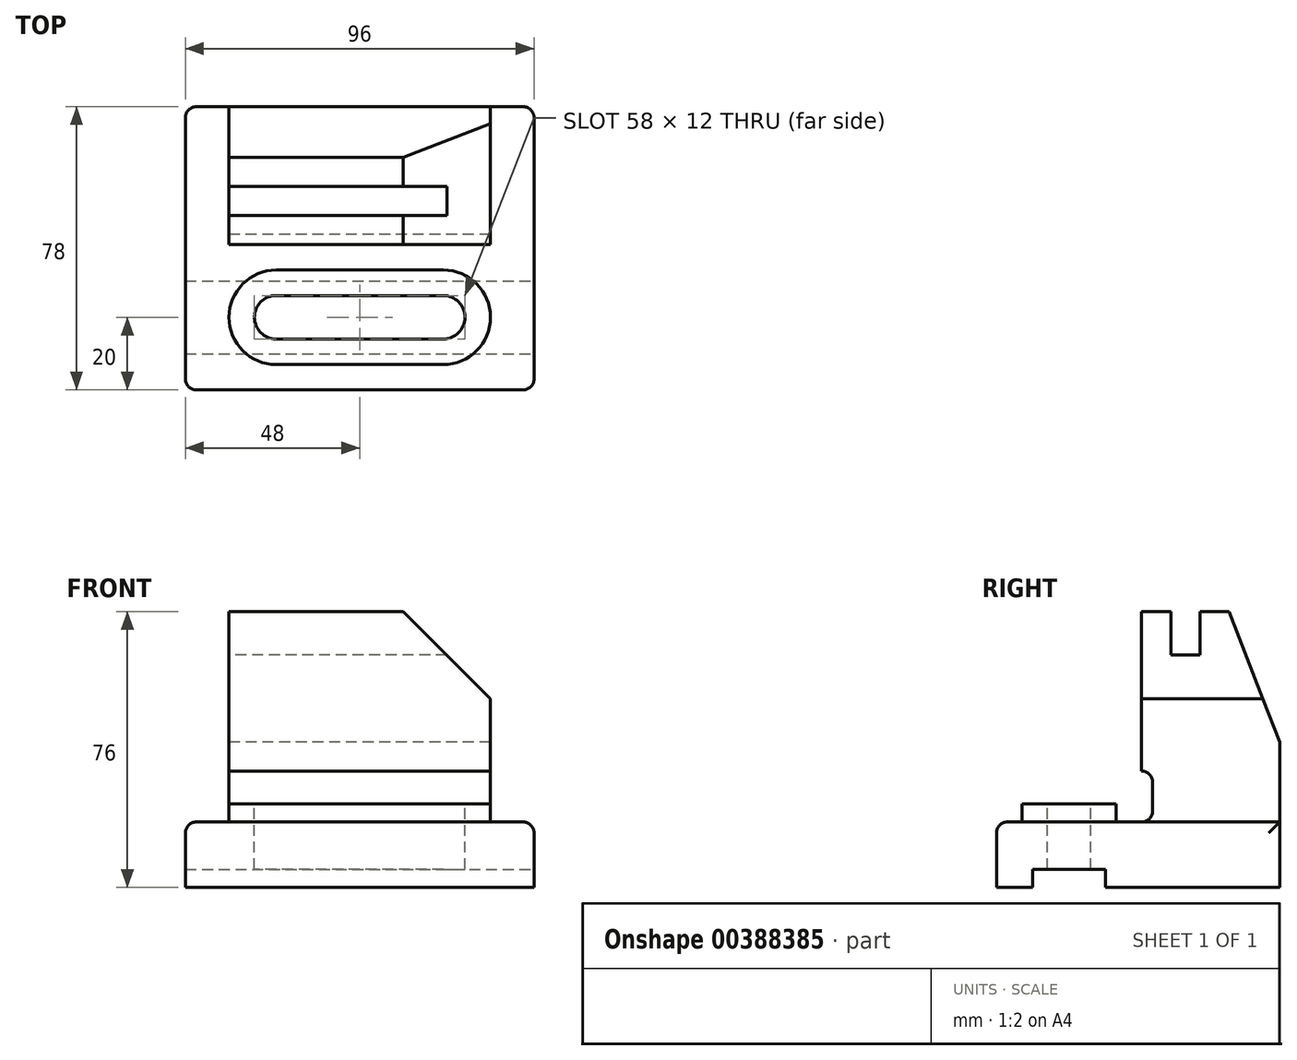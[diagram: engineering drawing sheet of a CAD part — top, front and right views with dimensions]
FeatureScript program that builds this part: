
annotation { "Feature Type Name" : "Feature", "Feature Type Description" : "" }
export const myFeature = defineFeature(function(context is Context, id is Id, definition is map)
    precondition{}
    {
        {
            var Q0;
            Q0=qCreatedBy(makeId("Top.planeOp"),FACE);
            var sketch = newSketch(context, id + "F0", { "sketchPlane" : qUnion([Q0])});
            skLineSegment(sketch, "E0.bottom", {"start": v(0, 0) * mm, "end": v(96, 0) * mm});
            skLineSegment(sketch, "E0.top", {"start": v(0, 78) * mm, "end": v(96, 78) * mm});
            skLineSegment(sketch, "E0.left", {"start": v(0, 0) * mm, "end": v(0, 78) * mm});
            skLineSegment(sketch, "E0.right", {"start": v(96, 0) * mm, "end": v(96, 78) * mm});
            skSolve(sketch);
        }
        {
            var Q0;
            Q0 = qSketchRegion(id + "F0", true);
            extrude(context, id + "F1", {"entities" : qUnion([Q0]), "depth" : 18 * mm});
        }
        {
            var Q0;
            Q0=makeQuery(id+"F1.opExtrude","CAP_FACE",FACE,{"disambiguationData":[OSD([sQuery(id+"F0.wireOp",EDGE,"E0.bottom"),sQuery(id+"F0.wireOp",EDGE,"E0.top"),sQuery(id+"F0.wireOp",EDGE,"E0.left"),sQuery(id+"F0.wireOp",EDGE,"E0.right")])],"isStart":false});
            var sketch = newSketch(context, id + "F2", { "sketchPlane" : qUnion([Q0])});
            skLineSegment(sketch, "E1.bottom", {"start": v(12, 78) * mm, "end": v(84, 78) * mm});
            skLineSegment(sketch, "E1.top", {"start": v(12, 40) * mm, "end": v(84, 40) * mm});
            skLineSegment(sketch, "E1.left", {"start": v(12, 78) * mm, "end": v(12, 40) * mm});
            skLineSegment(sketch, "E1.right", {"start": v(84, 78) * mm, "end": v(84, 40) * mm});
            skSolve(sketch);
        }
        {
            var Q0;
            Q0=makeQuery(id+"F1.opExtrude","CAP_FACE",FACE,{"disambiguationData":[OSD([sQuery(id+"F0.wireOp",EDGE,"E0.bottom"),sQuery(id+"F0.wireOp",EDGE,"E0.top"),sQuery(id+"F0.wireOp",EDGE,"E0.left"),sQuery(id+"F0.wireOp",EDGE,"E0.right")])],"isStart":true});
            cPlane(context, id + "F3", {"entities" : qUnion([Q0]), "cplaneType" : CPlaneType.OFFSET, "offset" : 76 * mm, "oppositeDirection" : true, "width" : 150 * mm, "height" : 150 * mm});
        }
        {
            var Q0;
            Q0=makeQuery(id+"F2.imprint","IMPRINT",FACE,{"disambiguationData":[TD([[makeQuery(id+"F2.imprint","IMPRINT",EDGE,{"derivedFrom":sQuery(id+"F2.wireOp",EDGE,"E1.bottom")}),-1.0]])]});
            var Q1;
            Q1=qCreatedBy(id+"F3.planeOp",FACE);
            extrude(context, id + "F4", {"entities" : qUnion([Q0]), "operationType" : NewBodyOperationType.ADD, "endBound" : BoundingType.UP_TO_SURFACE, "endBoundEntityFace" : qUnion([Q1]), "depth" : 9 * mm});
        }
        {
            var Q0;
            Q0=makeQuery(id+"F4.boolean.opBoolean","MERGE",FACE,{"derivedFrom":[makeQuery(id+"F1.opExtrude","SWEPT_FACE",FACE,{"disambiguationData":[OSD([sQuery(id+"F0.wireOp",EDGE,"E0.top")])]}),makeQuery(id+"F4.opExtrude","SWEPT_FACE",FACE,{"disambiguationData":[OSD([sQuery(id+"F2.wireOp",EDGE,"E1.bottom")])]})]});
            var sketch = newSketch(context, id + "F5", { "sketchPlane" : qUnion([Q0])});
            skLineSegment(sketch, "E2", {"start": v(-84, 76) * mm, "end": v(-60, 76) * mm});
            skLineSegment(sketch, "E3", {"start": v(-60, 76) * mm, "end": v(-84, 52) * mm});
            skLineSegment(sketch, "E4", {"start": v(-84, 52) * mm, "end": v(-84, 76) * mm});
            skSolve(sketch);
        }
        {
            var Q0;
            Q0 = qSketchRegion(id + "F5", true);
            var Q1;
            Q1=makeQuery(id+"F4.opExtrude","SWEPT_FACE",FACE,{"disambiguationData":[OSD([sQuery(id+"F2.wireOp",EDGE,"E1.top")])]});
            extrude(context, id + "F6", {"entities" : qUnion([Q0]), "operationType" : NewBodyOperationType.REMOVE, "endBound" : BoundingType.UP_TO_SURFACE, "oppositeDirection" : true, "endBoundEntityFace" : qUnion([Q1]), "depth" : 25 * mm});
        }
        {
            var Q0;
            Q0=makeQuery(id+"F4.opExtrude","SWEPT_FACE",FACE,{"disambiguationData":[OSD([sQuery(id+"F2.wireOp",EDGE,"E1.left")])]});
            var sketch = newSketch(context, id + "F7", { "sketchPlane" : qUnion([Q0])});
            skLineSegment(sketch, "E5.bottom", {"start": v(-48, 76) * mm, "end": v(-56, 76) * mm});
            skLineSegment(sketch, "E5.top", {"start": v(-48, 64) * mm, "end": v(-56, 64) * mm});
            skLineSegment(sketch, "E5.left", {"start": v(-48, 76) * mm, "end": v(-48, 64) * mm});
            skLineSegment(sketch, "E5.right", {"start": v(-56, 76) * mm, "end": v(-56, 64) * mm});
            skSolve(sketch);
        }
        {
            var Q0;
            Q0 = qSketchRegion(id + "F7", true);
            extrude(context, id + "F8", {"entities" : qUnion([Q0]), "operationType" : NewBodyOperationType.REMOVE, "endBound" : BoundingType.UP_TO_NEXT, "oppositeDirection" : true, "depth" : 25 * mm});
        }
        {
            var Q0;
            Q0=makeQuery(id+"F4.opExtrude","SWEPT_FACE",FACE,{"disambiguationData":[OSD([sQuery(id+"F2.wireOp",EDGE,"E1.left")])]});
            var sketch = newSketch(context, id + "F9", { "sketchPlane" : qUnion([Q0])});
            skLineSegment(sketch, "E6", {"start": v(-64, 76) * mm, "end": v(-78, 76) * mm});
            skLineSegment(sketch, "E7", {"start": v(-78, 76) * mm, "end": v(-78, 40) * mm});
            skLineSegment(sketch, "E8", {"start": v(-78, 40) * mm, "end": v(-64, 76) * mm});
            skSolve(sketch);
        }
        {
            var Q0;
            Q0 = qSketchRegion(id + "F9", true);
            extrude(context, id + "F10", {"entities" : qUnion([Q0]), "operationType" : NewBodyOperationType.REMOVE, "endBound" : BoundingType.UP_TO_NEXT, "oppositeDirection" : true, "depth" : 25 * mm});
        }
        {
            var Q0;
            Q0=makeQuery(id+"F1.opExtrude","SWEPT_FACE",FACE,{"disambiguationData":[OSD([sQuery(id+"F0.wireOp",EDGE,"E0.right")])]});
            var sketch = newSketch(context, id + "F11", { "sketchPlane" : qUnion([Q0])});
            skLineSegment(sketch, "E9.bottom", {"start": v(10, 0) * mm, "end": v(30, 0) * mm});
            skLineSegment(sketch, "E9.top", {"start": v(10, 5) * mm, "end": v(30, 5) * mm});
            skLineSegment(sketch, "E9.left", {"start": v(10, 0) * mm, "end": v(10, 5) * mm});
            skLineSegment(sketch, "E9.right", {"start": v(30, 0) * mm, "end": v(30, 5) * mm});
            skPoint(sketch, "E10", {"position": v(20, 5) * mm});
            skSolve(sketch);
        }
        {
            var Q0;
            Q0 = qSketchRegion(id + "F11", true);
            extrude(context, id + "F12", {"entities" : qUnion([Q0]), "operationType" : NewBodyOperationType.REMOVE, "endBound" : BoundingType.THROUGH_ALL, "oppositeDirection" : true, "depth" : 25 * mm});
        }
        {
            var Q0;
            Q0=makeQuery(id+"F1.opExtrude","CAP_FACE",FACE,{"disambiguationData":[OSD([sQuery(id+"F0.wireOp",EDGE,"E0.bottom"),sQuery(id+"F0.wireOp",EDGE,"E0.top"),sQuery(id+"F0.wireOp",EDGE,"E0.left"),sQuery(id+"F0.wireOp",EDGE,"E0.right")])],"isStart":false});
            var sketch = newSketch(context, id + "F13", { "sketchPlane" : qUnion([Q0])});
            skLineSegment(sketch, "E11.bottom", {"start": v(25, 33) * mm, "end": v(71, 33) * mm});
            skLineSegment(sketch, "E11.top", {"start": v(25, 7) * mm, "end": v(71, 7) * mm});
            skLineSegment(sketch, "E11.left", {"start": v(25, 33) * mm, "end": v(25, 7) * mm});
            skLineSegment(sketch, "E11.right", {"start": v(71, 33) * mm, "end": v(71, 7) * mm});
            skLineSegment(sketch, "E12", {"start": v(25, 20) * mm, "end": v(71, 20) * mm, "construction": true});
            skArc(sketch, "E13", {"start": v(25, 33) * mm, "mid": v(12, 20) * mm, "end": v(25, 7) * mm});
            skArc(sketch, "E14", {"start": v(71, 7) * mm, "mid": v(84, 20) * mm, "end": v(71, 33) * mm});
            skSolve(sketch);
        }
        {
            var Q0;
            Q0=makeQuery(id+"F13.imprint","IMPRINT",FACE,{"disambiguationData":[TD([[makeQuery(id+"F13.imprint","IMPRINT",EDGE,{"derivedFrom":sQuery(id+"F13.wireOp",EDGE,"E11.left")}),-1.0]])]});
            var Q1;
            Q1=makeQuery(id+"F13.imprint","IMPRINT",FACE,{"disambiguationData":[TD([[makeQuery(id+"F13.imprint","IMPRINT",EDGE,{"derivedFrom":sQuery(id+"F13.wireOp",EDGE,"E11.right")}),1.0]])]});
            var Q2;
            Q2=makeQuery(id+"F13.imprint","IMPRINT",FACE,{"disambiguationData":[TD([[makeQuery(id+"F13.imprint","IMPRINT",EDGE,{"derivedFrom":sQuery(id+"F13.wireOp",EDGE,"E11.bottom")}),-1.0]])]});
            extrude(context, id + "F14", {"entities" : qUnion([Q0, Q1, Q2]), "operationType" : NewBodyOperationType.ADD, "depth" : 5 * mm});
        }
        {
            var Q0;
            Q0=makeQuery(id+"F14.opExtrude","CAP_FACE",FACE,{"disambiguationData":[OSD([sQuery(id+"F13.wireOp",EDGE,"E11.bottom"),sQuery(id+"F13.wireOp",EDGE,"E11.top"),sQuery(id+"F13.wireOp",EDGE,"E13"),sQuery(id+"F13.wireOp",EDGE,"E14")])],"isStart":false});
            var sketch = newSketch(context, id + "F15", { "sketchPlane" : qUnion([Q0])});
            skLineSegment(sketch, "E15.JdR.JdR", {"start": v(25, 20) * mm, "end": v(71, 20) * mm, "construction": true});
            skArc(sketch, "E15.0.startCap", {"start": v(25, 14) * mm, "mid": v(19, 20) * mm, "end": v(25, 26) * mm});
            skArc(sketch, "E15.0.endCap", {"start": v(71, 26) * mm, "mid": v(77, 20) * mm, "end": v(71, 14) * mm});
            skLineSegment(sketch, "E15.0.left", {"start": v(25, 26) * mm, "end": v(71, 26) * mm});
            skLineSegment(sketch, "E15.0.right", {"start": v(25, 14) * mm, "end": v(71, 14) * mm});
            skSolve(sketch);
        }
        {
            var Q0;
            {var subQ0=sQuery(id+"F0.wireOp",EDGE,"E0.bottom");var subQ1=sQuery(id+"F0.wireOp",EDGE,"E0.right");var subQ2=sQuery(id+"F0.wireOp",EDGE,"E0.left");Q0=makeQuery(id+"F12.boolean.opBoolean","SPLIT",FACE,{"disambiguationData":[TD([makeQuery(id+"F1.opExtrude","SWEPT_FACE",FACE,{"disambiguationData":[OSD([subQ0])]})])],"derivedFrom":makeQuery(id+"F1.opExtrude","CAP_FACE",FACE,{"disambiguationData":[OSD([subQ0,sQuery(id+"F0.wireOp",EDGE,"E0.top"),subQ2,subQ1])],"isStart":true})});}
            cPlane(context, id + "F16", {"entities" : qUnion([Q0]), "cplaneType" : CPlaneType.OFFSET, "offset" : 20 * mm, "oppositeDirection" : true, "width" : 150 * mm, "height" : 150 * mm});
        }
        {
            var Q0;
            Q0 = qSketchRegion(id + "F15", true);
            var Q1;
            Q1=qCreatedBy(id+"F16.planeOp",FACE);
            extrude(context, id + "F17", {"entities" : qUnion([Q0]), "operationType" : NewBodyOperationType.REMOVE, "endBound" : BoundingType.THROUGH_ALL, "oppositeDirection" : true, "endBoundEntityFace" : qUnion([Q1]), "depth" : 25 * mm});
        }
        {
            var Q0;
            Q0=makeQuery(id+"F4.opExtrude","SWEPT_FACE",FACE,{"disambiguationData":[OSD([sQuery(id+"F2.wireOp",EDGE,"E1.right")])]});
            var sketch = newSketch(context, id + "F18", { "sketchPlane" : qUnion([Q0])});
            skLineSegment(sketch, "E16.bottom", {"start": v(40, 18) * mm, "end": v(43, 18) * mm});
            skLineSegment(sketch, "E16.top", {"start": v(40, 32) * mm, "end": v(43, 32) * mm});
            skLineSegment(sketch, "E16.left", {"start": v(40, 18) * mm, "end": v(40, 32) * mm});
            skLineSegment(sketch, "E16.right", {"start": v(43, 18) * mm, "end": v(43, 32) * mm});
            skSolve(sketch);
        }
        {
            var Q0;
            Q0 = qSketchRegion(id + "F18", true);
            extrude(context, id + "F19", {"entities" : qUnion([Q0]), "operationType" : NewBodyOperationType.REMOVE, "endBound" : BoundingType.UP_TO_NEXT, "oppositeDirection" : true, "depth" : 25 * mm});
        }
        {
            var Q0;
            Q0=makeQuery(id+"F14.opExtrude","CAP_EDGE",EDGE,{"disambiguationData":[OSD([sQuery(id+"F13.wireOp",EDGE,"E11.top")])],"isStart":true});
            var Q1;
            Q1=makeQuery(id+"F19.boolean.opBoolean","COPY",EDGE,{"derivedFrom":makeQuery(id+"F19.opExtrude","SWEPT_EDGE",EDGE,{"disambiguationData":[OSD([sQuery(id+"F2.wireOp",EDGE,"E1.right"),sQuery(id+"F18.wireOp",EDGE,"E16.bottom"),sQuery(id+"F18.wireOp",EDGE,"E16.right")])]})});
            var Q2;
            Q2=makeQuery(id+"F19.boolean.opBoolean","COPY",EDGE,{"derivedFrom":makeQuery(id+"F19.opExtrude","SWEPT_EDGE",EDGE,{"disambiguationData":[OSD([sQuery(id+"F18.wireOp",EDGE,"E16.top"),sQuery(id+"F18.wireOp",EDGE,"E16.right")])]})});
            var Q3;
            Q3=makeQuery(id+"F1.opExtrude","CAP_EDGE",EDGE,{"disambiguationData":[OSD([sQuery(id+"F0.wireOp",EDGE,"E0.bottom")])],"isStart":false});
            var Q4;
            Q4=makeQuery(id+"F1.opExtrude","CAP_EDGE",EDGE,{"disambiguationData":[OSD([sQuery(id+"F0.wireOp",EDGE,"E0.left")])],"isStart":false});
            var Q5;
            Q5=makeQuery(id+"F4.opExtrude","CAP_EDGE",EDGE,{"disambiguationData":[OSD([sQuery(id+"F2.wireOp",EDGE,"E1.right")])],"isStart":true});
            var Q6;
            Q6=makeQuery(id+"F4.opExtrude","CAP_EDGE",EDGE,{"disambiguationData":[OSD([sQuery(id+"F2.wireOp",EDGE,"E1.left")])],"isStart":true});
            var Q7;
            Q7=makeQuery(id+"F1.opExtrude","CAP_EDGE",EDGE,{"disambiguationData":[OSD([sQuery(id+"F0.wireOp",EDGE,"E0.right")])],"isStart":false});
            var Q8;
            Q8=makeQuery(id+"F1.opExtrude","SWEPT_EDGE",EDGE,{"disambiguationData":[OSD([sQuery(id+"F0.wireOp",EDGE,"E0.bottom"),sQuery(id+"F0.wireOp",EDGE,"E0.right")])]});
            var Q9;
            Q9=makeQuery(id+"F1.opExtrude","SWEPT_EDGE",EDGE,{"disambiguationData":[OSD([sQuery(id+"F0.wireOp",EDGE,"E0.bottom"),sQuery(id+"F0.wireOp",EDGE,"E0.left")])]});
            var Q10;
            Q10=makeQuery(id+"F1.opExtrude","SWEPT_EDGE",EDGE,{"disambiguationData":[OSD([sQuery(id+"F0.wireOp",EDGE,"E0.top"),sQuery(id+"F0.wireOp",EDGE,"E0.right")])]});
            var Q11;
            Q11=makeQuery(id+"F1.opExtrude","SWEPT_EDGE",EDGE,{"disambiguationData":[OSD([sQuery(id+"F0.wireOp",EDGE,"E0.top"),sQuery(id+"F0.wireOp",EDGE,"E0.left")])]});
            fillet(context, id + "F20", {"entities" : qUnion([Q0, Q1, Q2, Q3, Q4, Q5, Q6, Q7, Q8, Q9, Q10, Q11]), "radius" : 3 * mm, "tangentPropagation" : true, "allowEdgeOverflow" : false});
        }
    });
